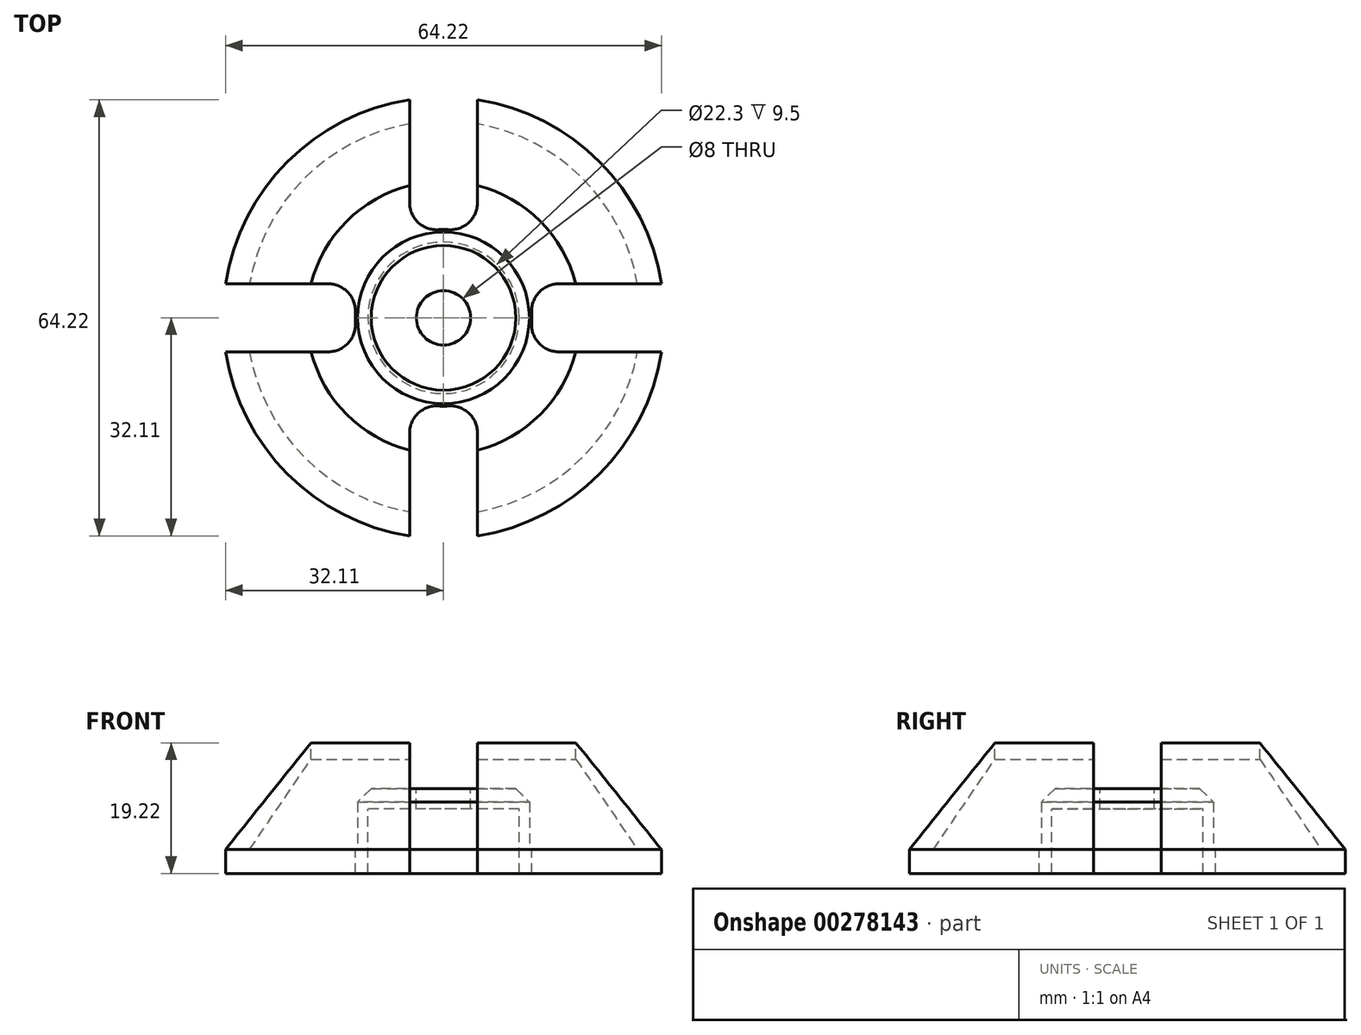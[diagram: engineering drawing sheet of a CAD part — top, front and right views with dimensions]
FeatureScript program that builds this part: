
annotation { "Feature Type Name" : "Feature", "Feature Type Description" : "" }
export const myFeature = defineFeature(function(context is Context, id is Id, definition is map)
    precondition{}
    {
        {
            var Q0;
            Q0=qCreatedBy(makeId("Top.planeOp"),FACE);
            var sketch = newSketch(context, id + "F0", { "sketchPlane" : qUnion([Q0])});
            skCircle(sketch, "E0", {"center": v(0, 0) * mm, "radius": 32.5 * mm});
            skCircle(sketch, "E1", {"center": v(0, 0) * mm, "radius": 12.65 * mm});
            skCircle(sketch, "E2", {"center": v(0, 0) * mm, "radius": 11.15 * mm});
            skSolve(sketch);
        }
        {
            var Q0;
            Q0=makeQuery(id+"F0.imprint","IMPRINT",FACE,{"disambiguationData":[TD([[makeQuery(id+"F0.imprint","IMPRINT",EDGE,{"derivedFrom":sQuery(id+"F0.wireOp",EDGE,"E0")}),1.0]])]});
            var Q1;
            Q1=makeQuery(id+"F0.imprint","IMPRINT",FACE,{"disambiguationData":[TD([[makeQuery(id+"F0.imprint","IMPRINT",EDGE,{"derivedFrom":sQuery(id+"F0.wireOp",EDGE,"E1")}),1.0]])]});
            extrude(context, id + "F1", {"entities" : qUnion([Q0, Q1]), "oppositeDirection" : true, "depth" : 3.5 * mm});
        }
        {
            var Q0;
            Q0=makeQuery(id+"F0.imprint","IMPRINT",FACE,{"disambiguationData":[TD([[makeQuery(id+"F0.imprint","IMPRINT",EDGE,{"derivedFrom":sQuery(id+"F0.wireOp",EDGE,"E1")}),1.0]])]});
            extrude(context, id + "F2", {"entities" : qUnion([Q0]), "operationType" : NewBodyOperationType.ADD, "depth" : (3 + 6) * mm});
        }
        {
            var Q0;
            Q0=makeQuery(id+"F2.opExtrude","CAP_FACE",FACE,{"disambiguationData":[OSD([sQuery(id+"F0.wireOp",EDGE,"E1"),sQuery(id+"F0.wireOp",EDGE,"E2")])],"isStart":false});
            var sketch = newSketch(context, id + "F3", { "sketchPlane" : qUnion([Q0])});
            skCircle(sketch, "E3", {"center": v(0, 0) * mm, "radius": 4 * mm});
            skSolve(sketch);
        }
        {
            var Q0;
            Q0=makeQuery(id+"F3.imprint","IMPRINT",FACE,{"disambiguationData":[TD([[makeQuery(id+"F3.imprint","IMPRINT",EDGE,{"derivedFrom":sQuery(id+"F3.wireOp",EDGE,"E3")}),-1.0]])]});
            extrude(context, id + "F4", {"entities" : qUnion([Q0]), "operationType" : NewBodyOperationType.ADD, "oppositeDirection" : true, "depth" : 3 * mm});
        }
        {
            var Q0;
            Q0=makeQuery(id+"F2.opExtrude","CAP_EDGE",EDGE,{"disambiguationData":[OSD([sQuery(id+"F0.wireOp",EDGE,"E1")])],"isStart":false});
            chamfer(context, id + "F5", {"entities" : qUnion([Q0]), "width" : 2 * mm, "tangentPropagation" : true});
        }
        {
            var Q0;
            Q0=qCreatedBy(makeId("Front.planeOp"),FACE);
            var sketch = newSketch(context, id + "F6", { "sketchPlane" : qUnion([Q0])});
            skLineSegment(sketch, "E4", {"start": v(-32.5, 0) * mm, "end": v(-20.13, 15.72) * mm});
            skLineSegment(sketch, "E5", {"start": v(-20.13, 15.72) * mm, "end": v(-20.13, 13.32) * mm});
            skLineSegment(sketch, "E6", {"start": v(-20.13, 13.32) * mm, "end": v(-29, 0) * mm});
            skLineSegment(sketch, "E7", {"start": v(-32.5, 0) * mm, "end": v(-29, 0) * mm});
            skSolve(sketch);
        }
        {
            var Q0;
            Q0=makeQuery(id+"F6.imprint","IMPRINT",FACE,{"disambiguationData":[TD([[makeQuery(id+"F6.imprint","IMPRINT",EDGE,{"derivedFrom":sQuery(id+"F6.wireOp",EDGE,"E4")}),-1.0]])]});
            var Q1;
            Q1=makeQuery(id+"F2.opExtrude","SWEPT_FACE",FACE,{"disambiguationData":[OSD([sQuery(id+"F0.wireOp",EDGE,"E1")])]});
            revolve(context, id + "F7", {"operationType" : NewBodyOperationType.ADD, "entities" : qUnion([Q0]), "axis" : qUnion([Q1]), "revolveType" : RevolveType.FULL});
        }
        {
            var Q0;
            Q0=qCreatedBy(makeId("Top.planeOp"),FACE);
            cPlane(context, id + "F8", {"entities" : qUnion([Q0]), "cplaneType" : CPlaneType.OFFSET, "offset" : 9 * mm, "width" : 150 * mm, "height" : 150 * mm});
        }
        {
            var Q0;
            Q0=qCreatedBy(id+"F8.planeOp",FACE);
            var sketch = newSketch(context, id + "F9", { "sketchPlane" : qUnion([Q0])});
            skLineSegment(sketch, "E8.bottom", {"start": v(-5, 35) * mm, "end": v(5, 35) * mm});
            skLineSegment(sketch, "E8.top", {"start": v(-5, -35) * mm, "end": v(5, -35) * mm});
            skLineSegment(sketch, "E8.left", {"start": v(-5, 35) * mm, "end": v(-5, -35) * mm});
            skLineSegment(sketch, "E8.right", {"start": v(5, 35) * mm, "end": v(5, -35) * mm});
            skPoint(sketch, "E8.middle", {"position": v(0, 0) * mm});
            skLineSegment(sketch, "E9.bottom", {"start": v(35, 5) * mm, "end": v(-35, 5) * mm});
            skLineSegment(sketch, "E9.top", {"start": v(35, -5) * mm, "end": v(-35, -5) * mm});
            skLineSegment(sketch, "E9.left", {"start": v(35, 5) * mm, "end": v(35, -5) * mm});
            skLineSegment(sketch, "E9.right", {"start": v(-35, 5) * mm, "end": v(-35, -5) * mm});
            skCircle(sketch, "E10", {"center": v(0, 0) * mm, "radius": 13 * mm});
            skSolve(sketch);
        }
        {
            var Q0;
            {var subQ0=sQuery(id+"F9.wireOp",EDGE,"E8.bottom");Q0=makeQuery(id+"F9.imprint","IMPRINT",FACE,{"disambiguationData":[TD([[makeQuery(id+"F9.imprint","IMPRINT",EDGE,{"derivedFrom":subQ0}),-1.0]])]});}
            var Q1;
            {var subQ0=sQuery(id+"F9.wireOp",EDGE,"E9.left");Q1=makeQuery(id+"F9.imprint","IMPRINT",FACE,{"disambiguationData":[TD([[makeQuery(id+"F9.imprint","IMPRINT",EDGE,{"derivedFrom":subQ0}),-1.0]])]});}
            var Q2;
            {var subQ0=sQuery(id+"F9.wireOp",EDGE,"E8.top");Q2=makeQuery(id+"F9.imprint","IMPRINT",FACE,{"disambiguationData":[TD([[makeQuery(id+"F9.imprint","IMPRINT",EDGE,{"derivedFrom":subQ0}),1.0]])]});}
            var Q3;
            {var subQ0=sQuery(id+"F9.wireOp",EDGE,"E9.right");Q3=makeQuery(id+"F9.imprint","IMPRINT",FACE,{"disambiguationData":[TD([[makeQuery(id+"F9.imprint","IMPRINT",EDGE,{"derivedFrom":subQ0}),1.0]])]});}
            extrude(context, id + "F10", {"entities" : qUnion([Q0, Q1, Q2, Q3]), "operationType" : NewBodyOperationType.REMOVE, "depth" : 25 * mm});
        }
        {
            var Q0;
            {var subQ0=sQuery(id+"F9.wireOp",EDGE,"E8.top");Q0=makeQuery(id+"F9.imprint","IMPRINT",FACE,{"disambiguationData":[TD([[makeQuery(id+"F9.imprint","IMPRINT",EDGE,{"derivedFrom":subQ0}),1.0]])]});}
            var Q1;
            {var subQ0=sQuery(id+"F9.wireOp",EDGE,"E8.bottom");Q1=makeQuery(id+"F9.imprint","IMPRINT",FACE,{"disambiguationData":[TD([[makeQuery(id+"F9.imprint","IMPRINT",EDGE,{"derivedFrom":subQ0}),-1.0]])]});}
            var Q2;
            {var subQ0=sQuery(id+"F9.wireOp",EDGE,"E9.right");Q2=makeQuery(id+"F9.imprint","IMPRINT",FACE,{"disambiguationData":[TD([[makeQuery(id+"F9.imprint","IMPRINT",EDGE,{"derivedFrom":subQ0}),1.0]])]});}
            var Q3;
            {var subQ0=sQuery(id+"F9.wireOp",EDGE,"E9.left");Q3=makeQuery(id+"F9.imprint","IMPRINT",FACE,{"disambiguationData":[TD([[makeQuery(id+"F9.imprint","IMPRINT",EDGE,{"derivedFrom":subQ0}),-1.0]])]});}
            extrude(context, id + "F11", {"entities" : qUnion([Q0, Q1, Q2, Q3]), "operationType" : NewBodyOperationType.REMOVE, "oppositeDirection" : true, "depth" : 15.2 * mm});
        }
        {
            var Q0;
            {var subQ0=sQuery(id+"F9.wireOp",EDGE,"E10");var subQ1=sQuery(id+"F9.wireOp",EDGE,"E9.bottom");Q0=makeQuery(id+"F11.boolean.opBoolean","COPY",EDGE,{"derivedFrom":makeQuery(id+"F11.opExtrude","SWEPT_EDGE",EDGE,{"disambiguationData":[OSD([subQ1,subQ0]),TDD([makeQuery(id+"F9.imprint","INTERSECT",VERTEX,{"disambiguationData":[OD(1.0)],"derivedFrom":[subQ1,subQ0]})])]})});}
            var Q1;
            {var subQ0=sQuery(id+"F9.wireOp",EDGE,"E10");var subQ1=sQuery(id+"F9.wireOp",EDGE,"E9.top");Q1=makeQuery(id+"F11.boolean.opBoolean","COPY",EDGE,{"derivedFrom":makeQuery(id+"F11.opExtrude","SWEPT_EDGE",EDGE,{"disambiguationData":[OSD([subQ1,subQ0]),TDD([makeQuery(id+"F9.imprint","INTERSECT",VERTEX,{"disambiguationData":[OD(1.0)],"derivedFrom":[subQ1,subQ0]})])]})});}
            var Q2;
            {var subQ0=sQuery(id+"F9.wireOp",EDGE,"E10");var subQ1=sQuery(id+"F9.wireOp",EDGE,"E8.left");Q2=makeQuery(id+"F11.boolean.opBoolean","COPY",EDGE,{"derivedFrom":makeQuery(id+"F11.opExtrude","SWEPT_EDGE",EDGE,{"disambiguationData":[OSD([subQ1,subQ0]),TDD([makeQuery(id+"F9.imprint","INTERSECT",VERTEX,{"disambiguationData":[OD(0.0)],"derivedFrom":[subQ1,subQ0]})])]})});}
            var Q3;
            {var subQ0=sQuery(id+"F9.wireOp",EDGE,"E10");var subQ1=sQuery(id+"F9.wireOp",EDGE,"E8.right");Q3=makeQuery(id+"F11.boolean.opBoolean","COPY",EDGE,{"derivedFrom":makeQuery(id+"F11.opExtrude","SWEPT_EDGE",EDGE,{"disambiguationData":[OSD([subQ1,subQ0]),TDD([makeQuery(id+"F9.imprint","INTERSECT",VERTEX,{"disambiguationData":[OD(0.0)],"derivedFrom":[subQ1,subQ0]})])]})});}
            var Q4;
            {var subQ0=sQuery(id+"F9.wireOp",EDGE,"E10");var subQ1=sQuery(id+"F9.wireOp",EDGE,"E8.left");Q4=makeQuery(id+"F11.boolean.opBoolean","COPY",EDGE,{"derivedFrom":makeQuery(id+"F11.opExtrude","SWEPT_EDGE",EDGE,{"disambiguationData":[OSD([subQ1,subQ0]),TDD([makeQuery(id+"F9.imprint","INTERSECT",VERTEX,{"disambiguationData":[OD(1.0)],"derivedFrom":[subQ1,subQ0]})])]})});}
            var Q5;
            {var subQ0=sQuery(id+"F9.wireOp",EDGE,"E10");var subQ1=sQuery(id+"F9.wireOp",EDGE,"E8.right");Q5=makeQuery(id+"F11.boolean.opBoolean","COPY",EDGE,{"derivedFrom":makeQuery(id+"F11.opExtrude","SWEPT_EDGE",EDGE,{"disambiguationData":[OSD([subQ1,subQ0]),TDD([makeQuery(id+"F9.imprint","INTERSECT",VERTEX,{"disambiguationData":[OD(1.0)],"derivedFrom":[subQ1,subQ0]})])]})});}
            var Q6;
            {var subQ0=sQuery(id+"F9.wireOp",EDGE,"E10");var subQ1=sQuery(id+"F9.wireOp",EDGE,"E9.top");Q6=makeQuery(id+"F11.boolean.opBoolean","COPY",EDGE,{"derivedFrom":makeQuery(id+"F11.opExtrude","SWEPT_EDGE",EDGE,{"disambiguationData":[OSD([subQ1,subQ0]),TDD([makeQuery(id+"F9.imprint","INTERSECT",VERTEX,{"disambiguationData":[OD(0.0)],"derivedFrom":[subQ1,subQ0]})])]})});}
            var Q7;
            {var subQ0=sQuery(id+"F9.wireOp",EDGE,"E10");var subQ1=sQuery(id+"F9.wireOp",EDGE,"E9.bottom");Q7=makeQuery(id+"F11.boolean.opBoolean","COPY",EDGE,{"derivedFrom":makeQuery(id+"F11.opExtrude","SWEPT_EDGE",EDGE,{"disambiguationData":[OSD([subQ1,subQ0]),TDD([makeQuery(id+"F9.imprint","INTERSECT",VERTEX,{"disambiguationData":[OD(0.0)],"derivedFrom":[subQ1,subQ0]})])]})});}
            fillet(context, id + "F12", {"entities" : qUnion([Q0, Q1, Q2, Q3, Q4, Q5, Q6, Q7]), "radius" : 4 * mm, "tangentPropagation" : true, "allowEdgeOverflow" : false});
        }
    });
